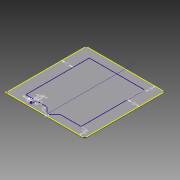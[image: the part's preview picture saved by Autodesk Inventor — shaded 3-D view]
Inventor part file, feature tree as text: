
AUTODESK INVENTOR PART (.ipt)
format: ipt  version: 2015 (Build 190159000, 159)  size: 102,400 bytes
history: native  units: mm
features: extrude x1, sketch x1
ambient origin geometry x8: Origin, YZ Plane, XZ Plane, XY Plane, X Axis, Y Axis, Z Axis, Center Point
bodies: Solid1 (feature_tree)
feature tree (2):
  extrude  "Extrusion1"  Depth=25.0mm
  sketch  "Sketch1"  dims[d17=0.0mm d30=25.0mm d31=4.0mm d32=4.0mm d33=4.0mm d34=4.0mm]
